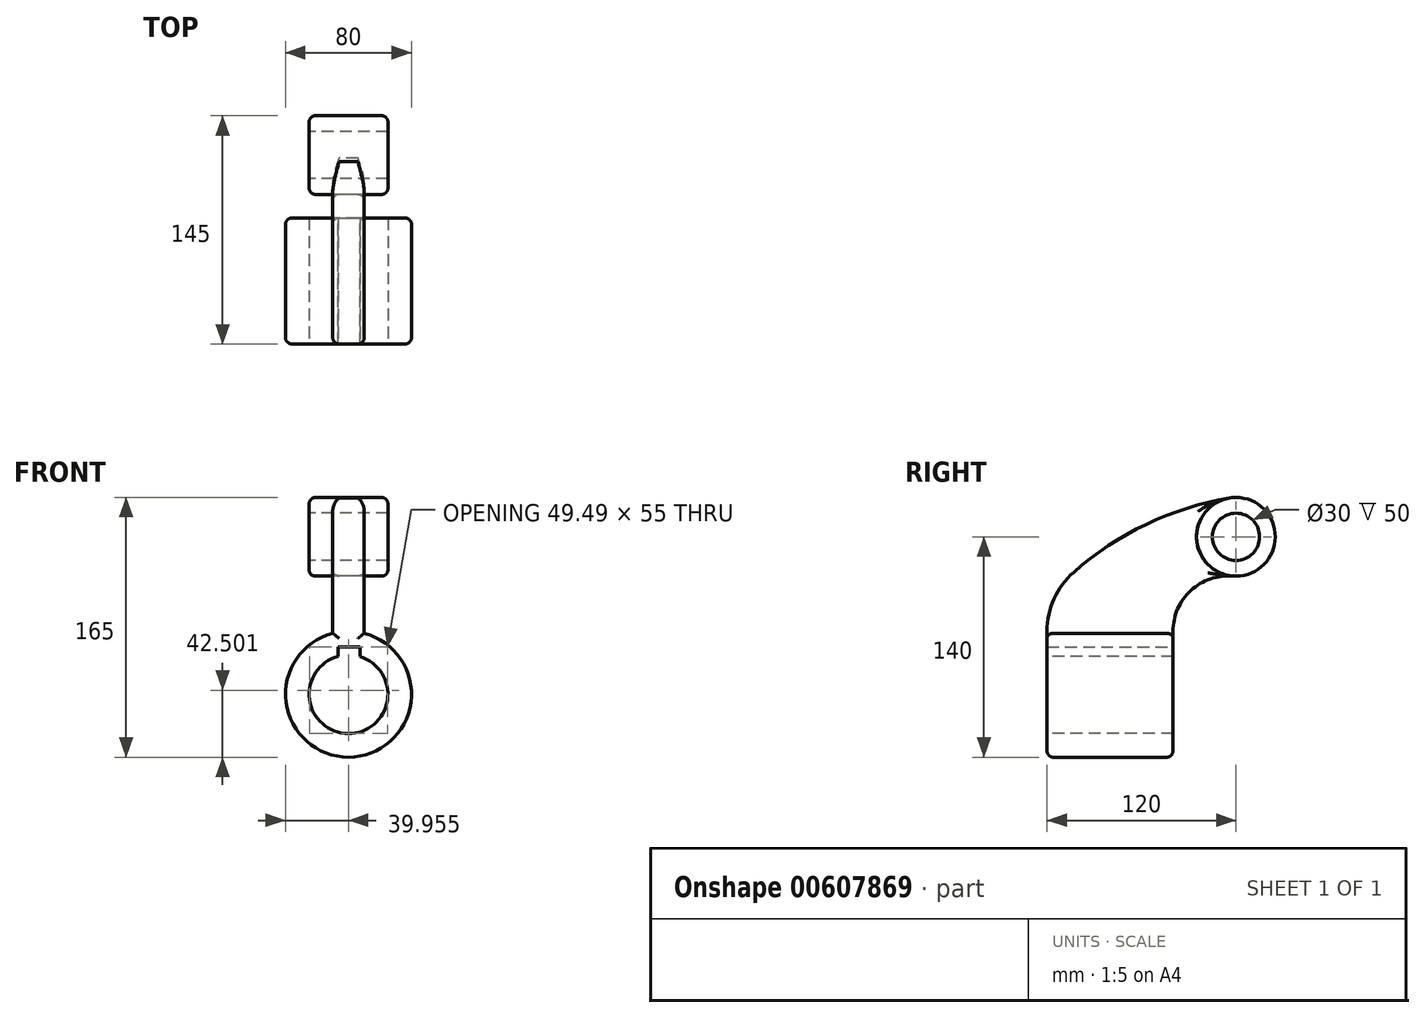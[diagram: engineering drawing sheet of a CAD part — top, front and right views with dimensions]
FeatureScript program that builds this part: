
annotation { "Feature Type Name" : "Feature", "Feature Type Description" : "" }
export const myFeature = defineFeature(function(context is Context, id is Id, definition is map)
    precondition{}
    {
        {
            var Q0;
            Q0=qCreatedBy(makeId("Right.planeOp"),FACE);
            var sketch = newSketch(context, id + "F0", { "sketchPlane" : qUnion([Q0])});
            skLineSegment(sketch, "E0.bottom", {"start": v(-80, 40) * mm, "end": v(0, 40) * mm});
            skLineSegment(sketch, "E0.top", {"start": v(-80, 25) * mm, "end": v(0, 25) * mm});
            skLineSegment(sketch, "E0.left", {"start": v(-80, 40) * mm, "end": v(-80, 25) * mm});
            skLineSegment(sketch, "E0.right", {"start": v(0, 40) * mm, "end": v(0, 25) * mm});
            skLineSegment(sketch, "E1", {"start": v(-80.17, 0) * mm, "end": v(0, 0) * mm, "construction": true});
            skCircle(sketch, "E2", {"center": v(40, 100) * mm, "radius": 15 * mm});
            skCircle(sketch, "E3", {"center": v(40, 100) * mm, "radius": 25 * mm});
            skArc(sketch, "E4", {"start": v(38, 75.08) * mm, "mid": v(11.32, 65.86) * mm, "end": v(0, 40) * mm});
            skArc(sketch, "E5", {"start": v(-63.05, 77.52) * mm, "mid": v(-75.57, 60.58) * mm, "end": v(-80, 40) * mm});
            skArc(sketch, "E6", {"start": v(35.84, 124.65) * mm, "mid": v(-16.9, 107.99) * mm, "end": v(-63.05, 77.52) * mm});
            skSolve(sketch);
        }
        {
            var Q0;
            Q0=makeQuery(id+"F0.imprint","IMPRINT",FACE,{"disambiguationData":[TD([[makeQuery(id+"F0.imprint","IMPRINT",EDGE,{"derivedFrom":sQuery(id+"F0.wireOp",EDGE,"E0.bottom")}),-1.0]])]});
            var Q1;
            Q1=sQuery(id+"F0.wireOp",EDGE,"E1");
            revolve(context, id + "F1", {"entities" : qUnion([Q0]), "axis" : qUnion([Q1]), "revolveType" : RevolveType.FULL});
        }
        {
            var Q0;
            Q0=makeQuery(id+"F0.imprint","IMPRINT",FACE,{"disambiguationData":[TD([[makeQuery(id+"F0.imprint","IMPRINT",EDGE,{"derivedFrom":sQuery(id+"F0.wireOp",EDGE,"E0.bottom")}),1.0]])]});
            var Q1;
            Q1=makeQuery(id+"F0.imprint","IMPRINT",FACE,{"disambiguationData":[TD([[makeQuery(id+"F0.imprint","IMPRINT",EDGE,{"derivedFrom":sQuery(id+"F0.wireOp",EDGE,"E0.bottom")}),-1.0]])]});
            extrude(context, id + "F2", {"entities" : qUnion([Q0, Q1]), "operationType" : NewBodyOperationType.ADD, "endBound" : BoundingType.SYMMETRIC, "depth" : 20 * mm, "offsetDistance" : 25 * mm});
        }
        {
            var Q0;
            Q0=makeQuery(id+"F0.imprint","IMPRINT",FACE,{"disambiguationData":[TD([[makeQuery(id+"F0.imprint","IMPRINT",EDGE,{"derivedFrom":sQuery(id+"F0.wireOp",EDGE,"E2")}),-1.0]])]});
            extrude(context, id + "F3", {"entities" : qUnion([Q0]), "endBound" : BoundingType.SYMMETRIC, "depth" : 50 * mm, "offsetDistance" : 25 * mm});
        }
        {
            var Q0;
            Q0=makeQuery(id+"F2.opExtrude","CAP_EDGE",EDGE,{"disambiguationData":[OSD([sQuery(id+"F0.wireOp",EDGE,"E5")])],"isStart":false});
            var Q1;
            Q1=makeQuery(id+"F1.opRevolve","SWEPT_EDGE",EDGE,{"disambiguationData":[OSD([sQuery(id+"F0.wireOp",EDGE,"E0.bottom"),sQuery(id+"F0.wireOp",EDGE,"E0.left"),sQuery(id+"F0.wireOp",EDGE,"E5")])]});
            var Q2;
            Q2=makeQuery(id+"F2.opExtrude","CAP_EDGE",EDGE,{"disambiguationData":[OSD([sQuery(id+"F0.wireOp",EDGE,"E5")])],"isStart":true});
            var Q3;
            Q3=makeQuery(id+"F2.opExtrude","CAP_EDGE",EDGE,{"disambiguationData":[OSD([sQuery(id+"F0.wireOp",EDGE,"E3")])],"isStart":false});
            var Q4;
            Q4=makeQuery(id+"F2.opExtrude","CAP_EDGE",EDGE,{"disambiguationData":[OSD([sQuery(id+"F0.wireOp",EDGE,"E6")])],"isStart":true});
            var Q5;
            Q5=makeQuery(id+"F2.opExtrude","CAP_EDGE",EDGE,{"disambiguationData":[OSD([sQuery(id+"F0.wireOp",EDGE,"E6")])],"isStart":false});
            var Q6;
            Q6=makeQuery(id+"F2.opExtrude","CAP_EDGE",EDGE,{"disambiguationData":[OSD([sQuery(id+"F0.wireOp",EDGE,"E4")])],"isStart":false});
            var Q7;
            Q7=makeQuery(id+"F1.opRevolve","SWEPT_EDGE",EDGE,{"disambiguationData":[OSD([sQuery(id+"F0.wireOp",EDGE,"E0.bottom"),sQuery(id+"F0.wireOp",EDGE,"E0.right"),sQuery(id+"F0.wireOp",EDGE,"E4")])]});
            var Q8;
            Q8=makeQuery(id+"F2.opExtrude","CAP_EDGE",EDGE,{"disambiguationData":[OSD([sQuery(id+"F0.wireOp",EDGE,"E3")])],"isStart":true});
            var Q9;
            Q9=makeQuery(id+"F2.opExtrude","CAP_EDGE",EDGE,{"disambiguationData":[OSD([sQuery(id+"F0.wireOp",EDGE,"E4")])],"isStart":true});
            fillet(context, id + "F4", {"entities" : qUnion([Q0, Q1, Q2, Q3, Q4, Q5, Q6, Q7, Q8, Q9]), "radius" : 4 * mm, "tangentPropagation" : true, "allowEdgeOverflow" : false});
        }
        {
            var Q0;
            Q0=makeQuery(id+"F3.opExtrude","CAP_EDGE",EDGE,{"disambiguationData":[OSD([sQuery(id+"F0.wireOp",EDGE,"E3")])],"isStart":false});
            var Q1;
            Q1=makeQuery(id+"F3.opExtrude","CAP_EDGE",EDGE,{"disambiguationData":[OSD([sQuery(id+"F0.wireOp",EDGE,"E3")])],"isStart":true});
            fillet(context, id + "F5", {"entities" : qUnion([Q0, Q1]), "radius" : 4 * mm, "tangentPropagation" : true, "allowEdgeOverflow" : false});
        }
        {
            var Q0;
            Q0=qCreatedBy(makeId("Front.planeOp"),FACE);
            var sketch = newSketch(context, id + "F6", { "sketchPlane" : qUnion([Q0])});
            skLineSegment(sketch, "E7.bottom", {"start": v(-6.7, 30) * mm, "end": v(7.3, 30) * mm});
            skLineSegment(sketch, "E7.top", {"start": v(-6.7, 0) * mm, "end": v(7.3, 0) * mm});
            skLineSegment(sketch, "E7.left", {"start": v(-6.7, 30) * mm, "end": v(-6.7, 0) * mm});
            skLineSegment(sketch, "E7.right", {"start": v(7.3, 30) * mm, "end": v(7.3, 0) * mm});
            skSolve(sketch);
        }
        {
            var Q0;
            Q0=makeQuery(id+"F6.imprint","IMPRINT",FACE,{"disambiguationData":[TD([[makeQuery(id+"F6.imprint","IMPRINT",EDGE,{"derivedFrom":sQuery(id+"F6.wireOp",EDGE,"E7.bottom")}),-1.0]])]});
            extrude(context, id + "F7", {"entities" : qUnion([Q0]), "operationType" : NewBodyOperationType.REMOVE, "depth" : 80 * mm, "offsetDistance" : 25 * mm});
        }
    });
